# Revit family: QF_Kelvinator_738279_KCHRI25R1DFE_Reach_In_Back_Room_Freezer_31_Long
name_source: partatom
category: Specialty Equipment
units: mm (PartAtom-declared; Revit-internal decimal feet)

## family parameters
Always vertical = Yes
Cut with Voids When Loaded = No
Part Type = Normal
Room Calculation Point = No
Round Connector Dimension = Use Diameter
Shared = No
Work Plane-Based = No

## types (1)
- QF_Kelvinator_738279_KCHRI25R1DFE_Reach_In_Back_Room_Freezer_31_Long
    Apparent Power = 920 VA
    Conn Conduit = Yes
    Conn Plug = 5-15P
    Cycle = 60 Hz
    Default Elevation = 0"
    Depth = 28 3/4"
    Description = Reach In Back Room Freezer 31" Long
    Elec Conn Connection Height = 0"
    Elec Conn RI Height = 0"
    FL Amps = 8 A
    Foodservice Equipment Identifier = Yes
    HP = 3/4
    Height = 77 3/16"
    Identify Quantity as Lot = Yes
    Item Number = 738279
    Length = 30 9/16"
    Manufacturer = Kelvinator Commercial
    Max Overcurrent Protection = 0 A
    Min Ckt Ampacity = 0 A
    Model = 738279 (KCHRI25R1DFE)
    Number of Poles = 1
    Phase = 1
    Refrigerant Type = R290
    Volts = 115 V
    Watts = 920 W
    Weight in Pounds = 264.555

## geometry (parser evidence)
native form markers: Blend x2, Sweep x8
no freeform markers — native parametric forms only
